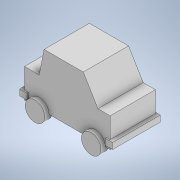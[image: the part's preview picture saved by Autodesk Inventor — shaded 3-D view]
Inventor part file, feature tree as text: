
AUTODESK INVENTOR PART (.ipt)
format: ipt  version: 2021 (Build 250183000, 183)  size: 176,128 bytes
history: native  units: mm
features: sketch x5, extrude x4, plane x2, other x2, mirror x1, surface_op x1
ambient origin geometry x8: Origin, YZ Plane, XZ Plane, XY Plane, X Axis, Y Axis, Z Axis, Center Point
bodies: Solid1 (feature_tree)
feature tree (15):
  extrude  "Extrusion1"  Depth=12.0mm
  extrude  "Extrusion2"  Depth=16.0mm
  extrude  "Extrusion3"  Depth=11.0mm
  plane  "Work Plane1"
  extrude  "Extrusion4"  Depth=18.5mm TaperAngle=0.0deg
  mirror  "Mirror1"
  plane  "Work Plane3"
  other  "Work Point1"
  sketch  "Sketch1"  dims[d0=35.0mm d1=12.0mm]
  sketch  "Sketch2"  dims[d2=16.0mm d3=6.0mm]
  sketch  "Sketch3"  dims[d4=5.0mm d5=11.0mm]
  sketch  "Sketch4"  dims[d6=16.0mm d7=18.5mm d8=0.0mm]
  sketch  "Sketch5"  dims[d9=8.0mm d10=8.0mm d11=6.0mm d12=23.0mm d13=22.0mm d14=0.0mm d15=16.0mm d16=3.0mm d17=35.0mm d18=0.0mm d19=1.5mm d20=2.5mm d21=19.5mm d22=0.5mm d23=3.0mm d24=0.0mm d25=-12.0mm d26=5.0mm]
  other  "Srf1"
  surface_op  "Boundary Patch1"
